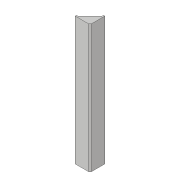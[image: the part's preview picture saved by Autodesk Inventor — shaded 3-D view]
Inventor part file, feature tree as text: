
AUTODESK INVENTOR PART (.ipt)
format: ipt  version: 2019 (Build 230136000, 136)  size: 95,232 bytes
history: native  units: in
note: dims shown in document units (in); Inventor stores cm internally (conversion verified against a paired STEP export)
features: sketch x3, extrude x2, other x2, loft x1
ambient origin geometry x8: Origin, YZ Plane, XZ Plane, XY Plane, X Axis, Y Axis, Z Axis, Center Point
bodies: Solid1 (feature_tree)
feature tree (8):
  extrude  "Extrusion1"  Depth=7.4803in
  sketch  "Sketch2"  dims[d2=0.0787in d3=0.0in d4=0.7874in]
  extrude  "Extrusion2"  Depth=0.7874in
  loft  "Loft1"
  sketch  "Sketch1"  dims[d0=0.7874in d1=7.4803in]
  sketch  "Sketch3"  dims[d5=7.4803in d6=0.0787in d7=0.0in d8=0.0in d9=90.0deg d10=0.0in d11=90.0deg]
  other  "Edges1"
  other  "Edges2"
